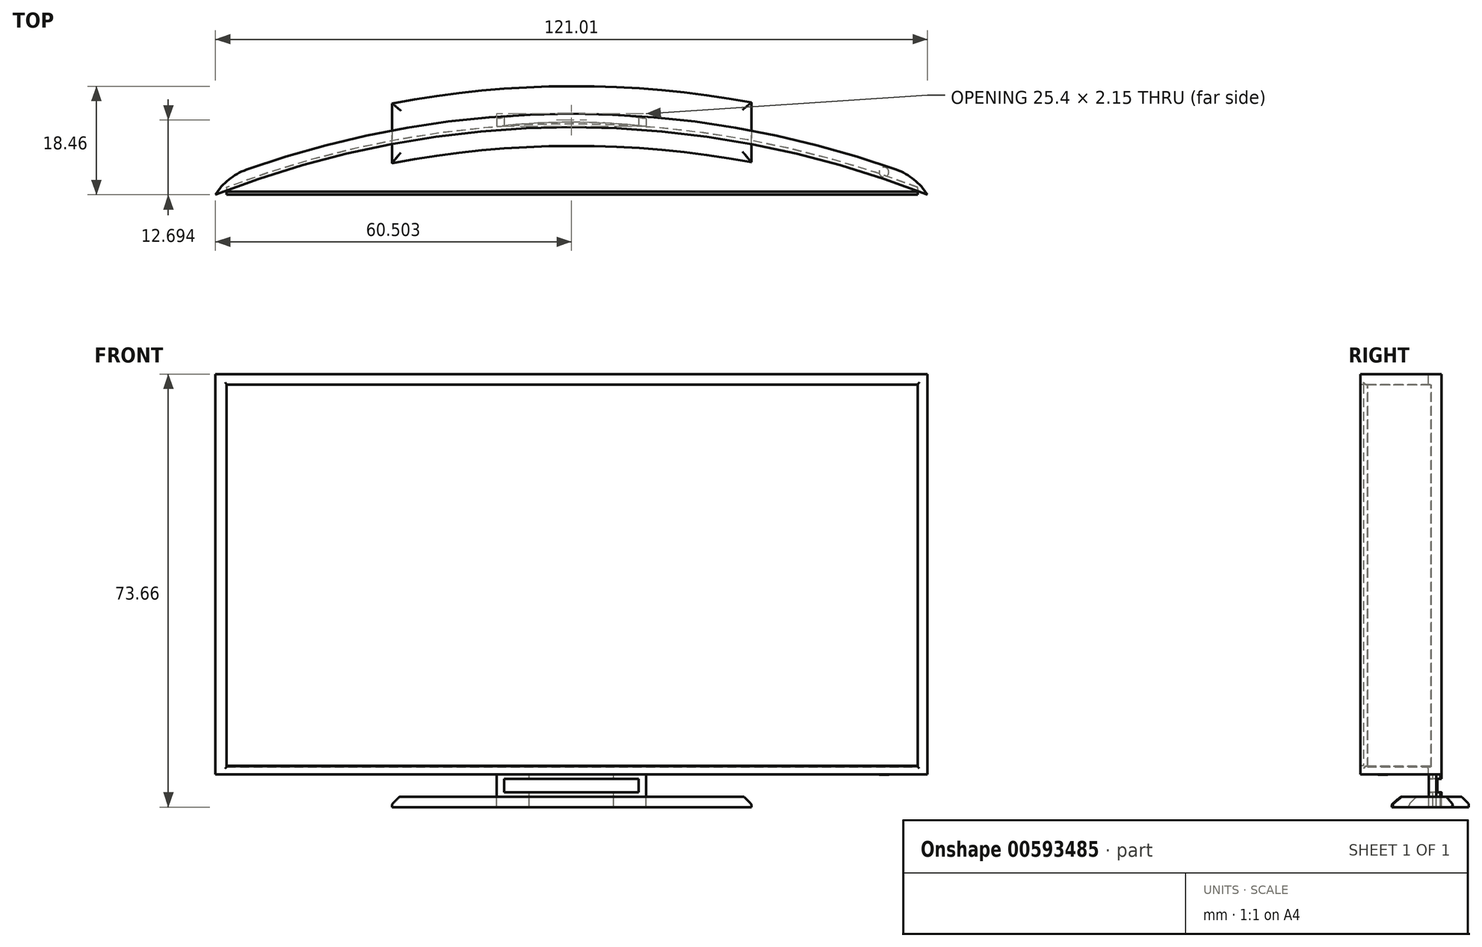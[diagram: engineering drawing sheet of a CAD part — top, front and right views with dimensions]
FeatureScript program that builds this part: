
annotation { "Feature Type Name" : "Feature", "Feature Type Description" : "" }
export const myFeature = defineFeature(function(context is Context, id is Id, definition is map)
    precondition{}
    {
        {
            var Q0;
            Q0=qCreatedBy(makeId("Top.planeOp"),FACE);
            var sketch = newSketch(context, id + "F0", { "sketchPlane" : qUnion([Q0])});
            skArc(sketch, "E0", {"start": v(60.54, 0) * mm, "mid": v(0.03, 11.49) * mm, "end": v(-60.47, 0) * mm});
            skLineSegment(sketch, "E1", {"start": v(-60.47, 0) * mm, "end": v(-60.47, 2.29) * mm});
            skLineSegment(sketch, "E2", {"start": v(60.54, 0) * mm, "end": v(60.54, 2.29) * mm});
            skArc(sketch, "E3", {"start": v(60.54, 2.29) * mm, "mid": v(0.03, 13.77) * mm, "end": v(-60.47, 2.29) * mm});
            skSolve(sketch);
        }
        {
            var Q0;
            Q0=makeQuery(id+"F0.imprint","IMPRINT",FACE,{"disambiguationData":[TD([[makeQuery(id+"F0.imprint","IMPRINT",EDGE,{"derivedFrom":sQuery(id+"F0.wireOp",EDGE,"E0")}),-1.0]])]});
            extrude(context, id + "F1", {"entities" : qUnion([Q0]), "depth" : 68.07 * mm, "offsetDistance" : 25.4 * mm});
        }
        {
            var Q0;
            Q0=makeQuery(id+"F1.opExtrude","SWEPT_EDGE",EDGE,{"disambiguationData":[OSD([sQuery(id+"F0.wireOp",EDGE,"E2"),sQuery(id+"F0.wireOp",EDGE,"E3")])]});
            fillet(context, id + "F2", {"entities" : qUnion([Q0]), "radius" : 10.16 * mm, "tangentPropagation" : true, "allowEdgeOverflow" : false});
        }
        {
            var Q0;
            Q0=makeQuery(id+"F1.opExtrude","SWEPT_EDGE",EDGE,{"disambiguationData":[OSD([sQuery(id+"F0.wireOp",EDGE,"E1"),sQuery(id+"F0.wireOp",EDGE,"E3")])]});
            fillet(context, id + "F3", {"entities" : qUnion([Q0]), "radius" : 10.16 * mm, "tangentPropagation" : true, "allowEdgeOverflow" : false});
        }
        {
            var Q0;
            Q0=makeQuery(id+"F1.opExtrude","CAP_FACE",FACE,{"disambiguationData":[OSD([sQuery(id+"F0.wireOp",EDGE,"E0"),sQuery(id+"F0.wireOp",EDGE,"E1"),sQuery(id+"F0.wireOp",EDGE,"E2"),sQuery(id+"F0.wireOp",EDGE,"E3")])],"isStart":true});
            var sketch = newSketch(context, id + "F4", { "sketchPlane" : qUnion([Q0])});
            skLineSegment(sketch, "E4", {"start": v(0.03, -12.89) * mm, "end": v(-12.67, -12.89) * mm, "construction": true});
            skPoint(sketch, "E4.startSnap0", {"position": v(0.03, -13.77) * mm});
            skLineSegment(sketch, "E5", {"start": v(0.03, -12.89) * mm, "end": v(12.73, -12.89) * mm, "construction": true});
            skArc(sketch, "E6", {"start": v(-12.67, -12.89) * mm, "mid": v(0.03, -13.95) * mm, "end": v(12.73, -12.89) * mm});
            skLineSegment(sketch, "E7", {"start": v(-12.67, -12.89) * mm, "end": v(-12.67, -11.62) * mm});
            skLineSegment(sketch, "E8", {"start": v(12.73, -12.89) * mm, "end": v(12.73, -11.62) * mm});
            skArc(sketch, "E9", {"start": v(-12.67, -11.62) * mm, "mid": v(0.03, -12.32) * mm, "end": v(12.73, -11.62) * mm});
            skSolve(sketch);
        }
        {
            var Q0;
            Q0=makeQuery(id+"F4.imprint","IMPRINT",FACE,{"disambiguationData":[TD([[makeQuery(id+"F4.imprint","IMPRINT",EDGE,{"derivedFrom":sQuery(id+"F4.wireOp",EDGE,"E6")}),1.0]])]});
            extrude(context, id + "F5", {"entities" : qUnion([Q0]), "operationType" : NewBodyOperationType.ADD, "depth" : 3.8 * mm, "offsetDistance" : 25.4 * mm});
        }
        {
            var Q0;
            Q0=qCreatedBy(makeId("Front.planeOp"),FACE);
            var sketch = newSketch(context, id + "F6", { "sketchPlane" : qUnion([Q0])});
            skLineSegment(sketch, "E10.bottom", {"start": v(-11.4, -0.76) * mm, "end": v(11.46, -0.76) * mm});
            skLineSegment(sketch, "E10.top", {"start": v(-11.4, -3.05) * mm, "end": v(11.46, -3.05) * mm});
            skLineSegment(sketch, "E10.left", {"start": v(-11.4, -0.76) * mm, "end": v(-11.4, -3.05) * mm});
            skLineSegment(sketch, "E10.right", {"start": v(11.46, -0.76) * mm, "end": v(11.46, -3.05) * mm});
            skSolve(sketch);
        }
        {
            var Q0;
            Q0=makeQuery(id+"F6.imprint","IMPRINT",FACE,{"disambiguationData":[TD([[makeQuery(id+"F6.imprint","IMPRINT",EDGE,{"derivedFrom":sQuery(id+"F6.wireOp",EDGE,"E10.bottom")}),-1.0]])]});
            extrude(context, id + "F7", {"entities" : qUnion([Q0]), "operationType" : NewBodyOperationType.REMOVE, "oppositeDirection" : true, "depth" : 25.4 * mm, "offsetDistance" : 25.4 * mm});
        }
        {
            var Q0;
            Q0=makeQuery(id+"F5.opExtrude","CAP_FACE",FACE,{"disambiguationData":[OSD([sQuery(id+"F4.wireOp",EDGE,"E6"),sQuery(id+"F4.wireOp",EDGE,"E7"),sQuery(id+"F4.wireOp",EDGE,"E8"),sQuery(id+"F4.wireOp",EDGE,"E9")])],"isStart":false});
            var sketch = newSketch(context, id + "F8", { "sketchPlane" : qUnion([Q0])});
            skPoint(sketch, "E11.startSnap0", {"position": v(-9.9, -13.3) * mm});
            skArc(sketch, "E12", {"start": v(-30.45, -15.54) * mm, "mid": v(0.08, -18.46) * mm, "end": v(30.61, -15.7) * mm});
            skLineSegment(sketch, "E13", {"start": v(-30.45, -15.54) * mm, "end": v(-30.45, -5.38) * mm});
            skLineSegment(sketch, "E14", {"start": v(30.61, -15.7) * mm, "end": v(30.61, -5.53) * mm});
            skArc(sketch, "E15", {"start": v(-30.45, -5.38) * mm, "mid": v(0.08, -8.3) * mm, "end": v(30.61, -5.53) * mm});
            skSolve(sketch);
        }
        {
            var Q0;
            Q0=makeQuery(id+"F8.imprint","IMPRINT",FACE,{"disambiguationData":[TD([[makeQuery(id+"F8.imprint","IMPRINT",EDGE,{"derivedFrom":sQuery(id+"F8.wireOp",EDGE,"E12")}),1.0]])]});
            extrude(context, id + "F9", {"entities" : qUnion([Q0]), "depth" : 1.78 * mm, "offsetDistance" : 25.4 * mm});
        }
        {
            var Q0;
            Q0=makeQuery(id+"F9.opExtrude","CAP_EDGE",EDGE,{"disambiguationData":[OSD([sQuery(id+"F8.wireOp",EDGE,"E15")])],"isStart":true});
            var Q1;
            Q1=makeQuery(id+"F9.opExtrude","CAP_EDGE",EDGE,{"disambiguationData":[OSD([sQuery(id+"F8.wireOp",EDGE,"E13")])],"isStart":true});
            var Q2;
            Q2=makeQuery(id+"F9.opExtrude","CAP_EDGE",EDGE,{"disambiguationData":[OSD([sQuery(id+"F8.wireOp",EDGE,"E14")])],"isStart":true});
            var Q3;
            Q3=makeQuery(id+"F9.opExtrude","CAP_EDGE",EDGE,{"disambiguationData":[OSD([sQuery(id+"F8.wireOp",EDGE,"E12")])],"isStart":true});
            chamfer(context, id + "F10", {"entities" : qUnion([Q0, Q1, Q2, Q3]), "width" : 1.27 * mm, "tangentPropagation" : true});
        }
        {
            var Q0;
            {var subQ0=sQuery(id+"F8.wireOp",EDGE,"E15");Q0=makeQuery(id+"F10.opChamfer","BLEND_EDGE",EDGE,{"blendedFrom":[makeQuery(id+"F9.opExtrude","CAP_EDGE",EDGE,{"disambiguationData":[OSD([subQ0])],"isStart":true}),makeQuery(id+"F9.opExtrude","SWEPT_FACE",FACE,{"disambiguationData":[OSD([subQ0])]})],"blendedInto":[makeQuery(id+"F9.opExtrude","SWEPT_FACE",FACE,{"disambiguationData":[OSD([subQ0])]})]});}
            var Q1;
            {var subQ0=sQuery(id+"F8.wireOp",EDGE,"E13");Q1=makeQuery(id+"F10.opChamfer","BLEND_EDGE",EDGE,{"blendedFrom":[makeQuery(id+"F9.opExtrude","CAP_EDGE",EDGE,{"disambiguationData":[OSD([subQ0])],"isStart":true}),makeQuery(id+"F9.opExtrude","SWEPT_FACE",FACE,{"disambiguationData":[OSD([subQ0])]})],"blendedInto":[makeQuery(id+"F9.opExtrude","SWEPT_FACE",FACE,{"disambiguationData":[OSD([subQ0])]})]});}
            var Q2;
            {var subQ0=sQuery(id+"F8.wireOp",EDGE,"E14");Q2=makeQuery(id+"F10.opChamfer","BLEND_EDGE",EDGE,{"blendedFrom":[makeQuery(id+"F9.opExtrude","CAP_EDGE",EDGE,{"disambiguationData":[OSD([subQ0])],"isStart":true}),makeQuery(id+"F9.opExtrude","SWEPT_FACE",FACE,{"disambiguationData":[OSD([subQ0])]})],"blendedInto":[makeQuery(id+"F9.opExtrude","SWEPT_FACE",FACE,{"disambiguationData":[OSD([subQ0])]})]});}
            var Q3;
            {var subQ0=sQuery(id+"F8.wireOp",EDGE,"E12");Q3=makeQuery(id+"F10.opChamfer","BLEND_EDGE",EDGE,{"blendedFrom":[makeQuery(id+"F9.opExtrude","CAP_EDGE",EDGE,{"disambiguationData":[OSD([subQ0])],"isStart":true}),makeQuery(id+"F9.opExtrude","SWEPT_FACE",FACE,{"disambiguationData":[OSD([subQ0])]})],"blendedInto":[makeQuery(id+"F9.opExtrude","SWEPT_FACE",FACE,{"disambiguationData":[OSD([subQ0])]})]});}
            var Q4;
            {var subQ0=sQuery(id+"F8.wireOp",EDGE,"E13");Q4=makeQuery(id+"F10.opChamfer","BLEND_EDGE",EDGE,{"blendedFrom":[makeQuery(id+"F9.opExtrude","CAP_EDGE",EDGE,{"disambiguationData":[OSD([subQ0])],"isStart":true}),makeQuery(id+"F9.opExtrude","CAP_FACE",FACE,{"disambiguationData":[OSD([sQuery(id+"F4.wireOp",EDGE,"E6"),sQuery(id+"F4.wireOp",EDGE,"E7"),sQuery(id+"F4.wireOp",EDGE,"E8"),sQuery(id+"F4.wireOp",EDGE,"E9"),sQuery(id+"F8.wireOp",EDGE,"E12"),subQ0,sQuery(id+"F8.wireOp",EDGE,"E14"),sQuery(id+"F8.wireOp",EDGE,"E15")])],"isStart":true})],"blendedInto":[makeQuery(id+"F9.opExtrude","CAP_FACE",FACE,{"disambiguationData":[OSD([sQuery(id+"F4.wireOp",EDGE,"E6"),sQuery(id+"F4.wireOp",EDGE,"E7"),sQuery(id+"F4.wireOp",EDGE,"E8"),sQuery(id+"F4.wireOp",EDGE,"E9"),sQuery(id+"F8.wireOp",EDGE,"E12"),subQ0,sQuery(id+"F8.wireOp",EDGE,"E14"),sQuery(id+"F8.wireOp",EDGE,"E15")])],"isStart":true})]});}
            var Q5;
            {var subQ0=sQuery(id+"F8.wireOp",EDGE,"E12");Q5=makeQuery(id+"F10.opChamfer","BLEND_EDGE",EDGE,{"blendedFrom":[makeQuery(id+"F9.opExtrude","CAP_EDGE",EDGE,{"disambiguationData":[OSD([subQ0])],"isStart":true}),makeQuery(id+"F9.opExtrude","CAP_FACE",FACE,{"disambiguationData":[OSD([sQuery(id+"F4.wireOp",EDGE,"E6"),sQuery(id+"F4.wireOp",EDGE,"E7"),sQuery(id+"F4.wireOp",EDGE,"E8"),sQuery(id+"F4.wireOp",EDGE,"E9"),subQ0,sQuery(id+"F8.wireOp",EDGE,"E13"),sQuery(id+"F8.wireOp",EDGE,"E14"),sQuery(id+"F8.wireOp",EDGE,"E15")])],"isStart":true})],"blendedInto":[makeQuery(id+"F9.opExtrude","CAP_FACE",FACE,{"disambiguationData":[OSD([sQuery(id+"F4.wireOp",EDGE,"E6"),sQuery(id+"F4.wireOp",EDGE,"E7"),sQuery(id+"F4.wireOp",EDGE,"E8"),sQuery(id+"F4.wireOp",EDGE,"E9"),subQ0,sQuery(id+"F8.wireOp",EDGE,"E13"),sQuery(id+"F8.wireOp",EDGE,"E14"),sQuery(id+"F8.wireOp",EDGE,"E15")])],"isStart":true})]});}
            var Q6;
            {var subQ0=sQuery(id+"F8.wireOp",EDGE,"E15");Q6=makeQuery(id+"F10.opChamfer","BLEND_EDGE",EDGE,{"blendedFrom":[makeQuery(id+"F9.opExtrude","CAP_EDGE",EDGE,{"disambiguationData":[OSD([subQ0])],"isStart":true}),makeQuery(id+"F9.opExtrude","CAP_FACE",FACE,{"disambiguationData":[OSD([sQuery(id+"F4.wireOp",EDGE,"E6"),sQuery(id+"F4.wireOp",EDGE,"E7"),sQuery(id+"F4.wireOp",EDGE,"E8"),sQuery(id+"F4.wireOp",EDGE,"E9"),sQuery(id+"F8.wireOp",EDGE,"E12"),sQuery(id+"F8.wireOp",EDGE,"E13"),sQuery(id+"F8.wireOp",EDGE,"E14"),subQ0])],"isStart":true})],"blendedInto":[makeQuery(id+"F9.opExtrude","CAP_FACE",FACE,{"disambiguationData":[OSD([sQuery(id+"F4.wireOp",EDGE,"E6"),sQuery(id+"F4.wireOp",EDGE,"E7"),sQuery(id+"F4.wireOp",EDGE,"E8"),sQuery(id+"F4.wireOp",EDGE,"E9"),sQuery(id+"F8.wireOp",EDGE,"E12"),sQuery(id+"F8.wireOp",EDGE,"E13"),sQuery(id+"F8.wireOp",EDGE,"E14"),subQ0])],"isStart":true})]});}
            var Q7;
            {var subQ0=sQuery(id+"F8.wireOp",EDGE,"E14");Q7=makeQuery(id+"F10.opChamfer","BLEND_EDGE",EDGE,{"blendedFrom":[makeQuery(id+"F9.opExtrude","CAP_EDGE",EDGE,{"disambiguationData":[OSD([subQ0])],"isStart":true}),makeQuery(id+"F9.opExtrude","CAP_FACE",FACE,{"disambiguationData":[OSD([sQuery(id+"F4.wireOp",EDGE,"E6"),sQuery(id+"F4.wireOp",EDGE,"E7"),sQuery(id+"F4.wireOp",EDGE,"E8"),sQuery(id+"F4.wireOp",EDGE,"E9"),sQuery(id+"F8.wireOp",EDGE,"E12"),sQuery(id+"F8.wireOp",EDGE,"E13"),subQ0,sQuery(id+"F8.wireOp",EDGE,"E15")])],"isStart":true})],"blendedInto":[makeQuery(id+"F9.opExtrude","CAP_FACE",FACE,{"disambiguationData":[OSD([sQuery(id+"F4.wireOp",EDGE,"E6"),sQuery(id+"F4.wireOp",EDGE,"E7"),sQuery(id+"F4.wireOp",EDGE,"E8"),sQuery(id+"F4.wireOp",EDGE,"E9"),sQuery(id+"F8.wireOp",EDGE,"E12"),sQuery(id+"F8.wireOp",EDGE,"E13"),subQ0,sQuery(id+"F8.wireOp",EDGE,"E15")])],"isStart":true})]});}
            fillet(context, id + "F11", {"entities" : qUnion([Q0, Q1, Q2, Q3, Q4, Q5, Q6, Q7]), "radius" : 0.5 * mm, "tangentPropagation" : true, "allowEdgeOverflow" : false});
        }
        {
            var Q0;
            Q0=qCreatedBy(makeId("Front.planeOp"),FACE);
            var sketch = newSketch(context, id + "F12", { "sketchPlane" : qUnion([Q0])});
            skLineSegment(sketch, "E16", {"start": v(-58.56, 66.24) * mm, "end": v(-58.56, 1.42) * mm});
            skLineSegment(sketch, "E17", {"start": v(58.9, 66.24) * mm, "end": v(58.9, 1.42) * mm});
            skLineSegment(sketch, "E18", {"start": v(-58.56, 66.24) * mm, "end": v(58.9, 66.24) * mm});
            skLineSegment(sketch, "E19", {"start": v(-58.56, 1.42) * mm, "end": v(58.9, 1.42) * mm});
            skSolve(sketch);
        }
        {
            var Q0;
            Q0=makeQuery(id+"F12.imprint","IMPRINT",FACE,{"disambiguationData":[TD([[makeQuery(id+"F12.imprint","IMPRINT",EDGE,{"derivedFrom":sQuery(id+"F12.wireOp",EDGE,"E16")}),1.0]])]});
            extrude(context, id + "F13", {"entities" : qUnion([Q0]), "oppositeDirection" : true, "depth" : 0.5 * mm, "offsetDistance" : 25.4 * mm});
        }
        {
            var Q0;
            Q0=makeQuery(id+"F13.opExtrude","SWEPT_FACE",FACE,{"disambiguationData":[OSD([sQuery(id+"F12.wireOp",EDGE,"E18")])]});
            var sketch = newSketch(context, id + "F14", { "sketchPlane" : qUnion([Q0])});
            skLineSegment(sketch, "E20", {"start": v(-58.56, 0) * mm, "end": v(-58.56, 1.27) * mm});
            skLineSegment(sketch, "E21", {"start": v(58.9, 0) * mm, "end": v(58.9, 1.27) * mm});
            skArc(sketch, "E22", {"start": v(58.9, 1.27) * mm, "mid": v(0.17, 12.07) * mm, "end": v(-58.56, 1.27) * mm});
            skSolve(sketch);
        }
        {
            var Q0;
            Q0=makeQuery(id+"F14.imprint","IMPRINT",FACE,{"disambiguationData":[TD([[makeQuery(id+"F14.imprint","IMPRINT",EDGE,{"derivedFrom":sQuery(id+"F14.wireOp",EDGE,"E20")}),-1.0]])]});
            extrude(context, id + "F15", {"entities" : qUnion([Q0]), "operationType" : NewBodyOperationType.REMOVE, "oppositeDirection" : true, "depth" : 64.87 * mm, "offsetDistance" : 25.4 * mm});
        }
        {
            var Q0;
            Q0=makeQuery(id+"F15.boolean.opBoolean","COPY",FACE,{"derivedFrom":makeQuery(id+"F15.opExtrude","CAP_FACE",FACE,{"disambiguationData":[OSD([sQuery(id+"F12.wireOp",EDGE,"E18"),sQuery(id+"F14.wireOp",EDGE,"E20"),sQuery(id+"F14.wireOp",EDGE,"E21"),sQuery(id+"F14.wireOp",EDGE,"E22")])],"isStart":true})});
            var sketch = newSketch(context, id + "F16", { "sketchPlane" : qUnion([Q0])});
            skLineSegment(sketch, "E23", {"start": v(-58.56, -1.27) * mm, "end": v(-58.56, -1.24) * mm});
            skLineSegment(sketch, "E24", {"start": v(58.9, -1.27) * mm, "end": v(58.9, -1.24) * mm});
            skArc(sketch, "E25", {"start": v(-58.56, -1.27) * mm, "mid": v(0.17, -12.07) * mm, "end": v(58.9, -1.27) * mm});
            skArc(sketch, "E26", {"start": v(-58.56, -1.24) * mm, "mid": v(0.17, -12.04) * mm, "end": v(58.9, -1.24) * mm});
            skSolve(sketch);
        }
        {
            var Q0;
            Q0=makeQuery(id+"F16.imprint","IMPRINT",FACE,{"disambiguationData":[TD([[makeQuery(id+"F16.imprint","IMPRINT",EDGE,{"derivedFrom":sQuery(id+"F16.wireOp",EDGE,"E23")}),1.0]])]});
            extrude(context, id + "F17", {"entities" : qUnion([Q0]), "depth" : 65.02 * mm, "offsetDistance" : 25.4 * mm});
        }
        {
            var Q0;
            Q0=makeQuery(id+"F15.boolean.opBoolean","INTERSECT",EDGE,{"derivedFrom":[makeQuery(id+"F1.opExtrude","SWEPT_FACE",FACE,{"disambiguationData":[OSD([sQuery(id+"F0.wireOp",EDGE,"E0")])]}),makeQuery(id+"F15.opExtrude","CAP_FACE",FACE,{"disambiguationData":[OSD([sQuery(id+"F12.wireOp",EDGE,"E18"),sQuery(id+"F14.wireOp",EDGE,"E20"),sQuery(id+"F14.wireOp",EDGE,"E21"),sQuery(id+"F14.wireOp",EDGE,"E22")])],"isStart":true})]});
            var Q1;
            Q1=makeQuery(id+"F15.boolean.opBoolean","INTERSECT",EDGE,{"derivedFrom":[makeQuery(id+"F1.opExtrude","SWEPT_FACE",FACE,{"disambiguationData":[OSD([sQuery(id+"F0.wireOp",EDGE,"E0")])]}),makeQuery(id+"F15.opExtrude","SWEPT_FACE",FACE,{"disambiguationData":[OSD([sQuery(id+"F14.wireOp",EDGE,"E20")])]})]});
            var Q2;
            Q2=makeQuery(id+"F15.boolean.opBoolean","INTERSECT",EDGE,{"derivedFrom":[makeQuery(id+"F1.opExtrude","SWEPT_FACE",FACE,{"disambiguationData":[OSD([sQuery(id+"F0.wireOp",EDGE,"E0")])]}),makeQuery(id+"F15.opExtrude","CAP_FACE",FACE,{"disambiguationData":[OSD([sQuery(id+"F12.wireOp",EDGE,"E18"),sQuery(id+"F14.wireOp",EDGE,"E20"),sQuery(id+"F14.wireOp",EDGE,"E21"),sQuery(id+"F14.wireOp",EDGE,"E22")])],"isStart":false})]});
            var Q3;
            Q3=makeQuery(id+"F15.boolean.opBoolean","INTERSECT",EDGE,{"derivedFrom":[makeQuery(id+"F1.opExtrude","SWEPT_FACE",FACE,{"disambiguationData":[OSD([sQuery(id+"F0.wireOp",EDGE,"E0")])]}),makeQuery(id+"F15.opExtrude","SWEPT_FACE",FACE,{"disambiguationData":[OSD([sQuery(id+"F14.wireOp",EDGE,"E21")])]})]});
            fillet(context, id + "F18", {"entities" : qUnion([Q0, Q1, Q2, Q3]), "radius" : 0.38 * mm, "tangentPropagation" : true, "allowEdgeOverflow" : false});
        }
        {
            var Q0;
            Q0=makeQuery(id+"F1.opExtrude","CAP_FACE",FACE,{"disambiguationData":[OSD([sQuery(id+"F0.wireOp",EDGE,"E0"),sQuery(id+"F0.wireOp",EDGE,"E1"),sQuery(id+"F0.wireOp",EDGE,"E2"),sQuery(id+"F0.wireOp",EDGE,"E3")])],"isStart":true});
            var sketch = newSketch(context, id + "F19", { "sketchPlane" : qUnion([Q0])});
            skCircle(sketch, "E27", {"center": v(53.15, -3.85) * mm, "radius": 0.82 * mm});
            skSolve(sketch);
        }
        {
            var Q0;
            Q0=makeQuery(id+"F19.imprint","IMPRINT",FACE,{"disambiguationData":[TD([[makeQuery(id+"F19.imprint","IMPRINT",EDGE,{"derivedFrom":sQuery(id+"F19.wireOp",EDGE,"E27")}),1.0]])]});
            extrude(context, id + "F20", {"entities" : qUnion([Q0]), "depth" : 0.08 * mm, "offsetDistance" : 25.4 * mm});
        }
    });
